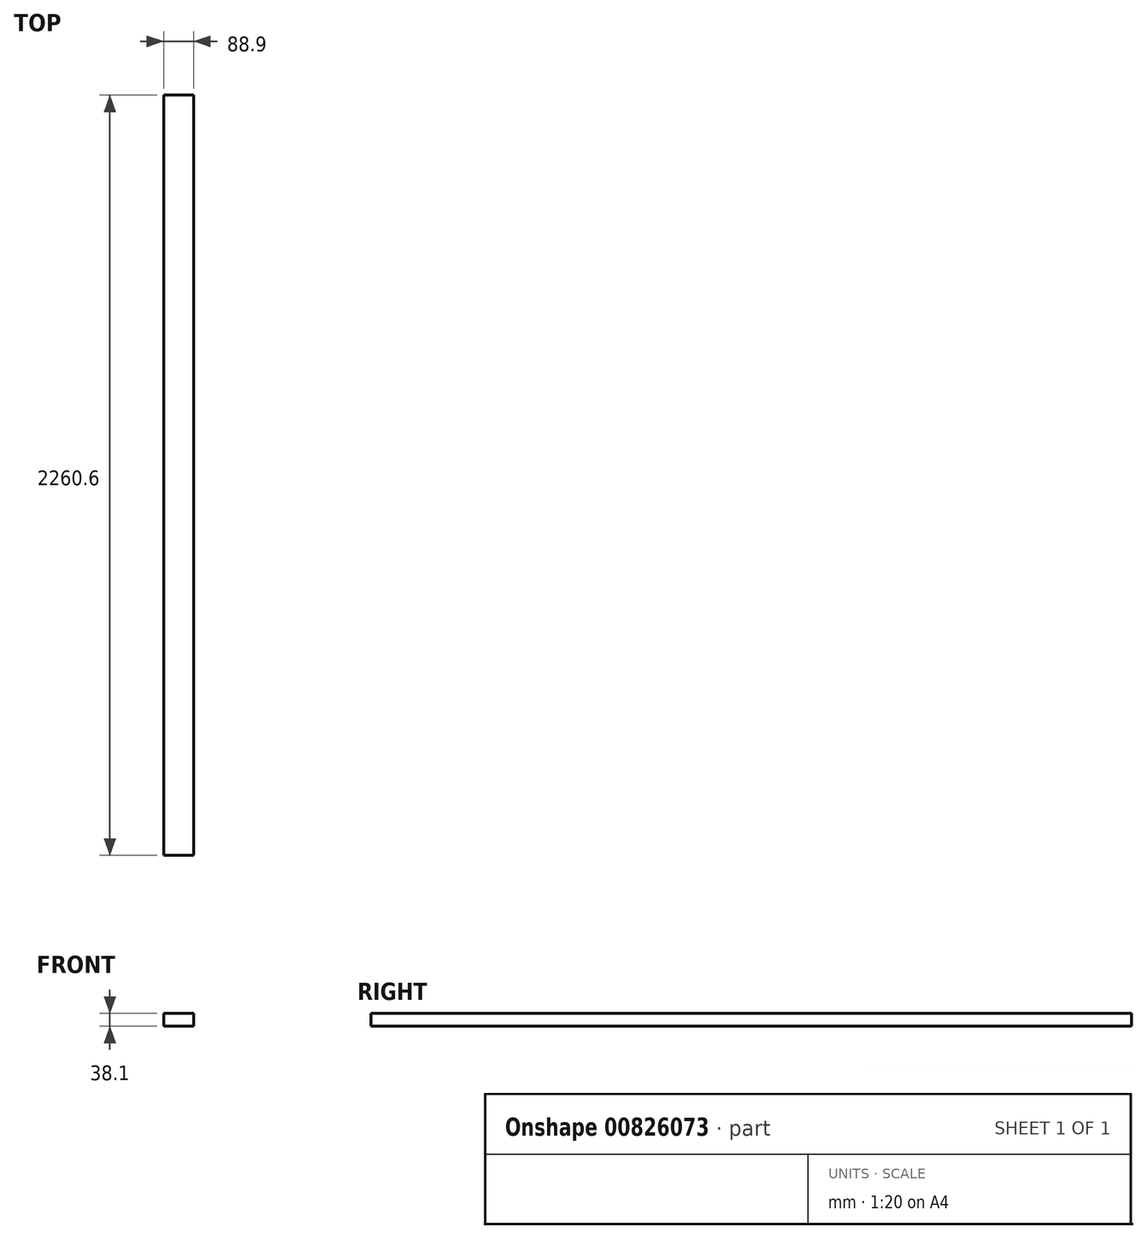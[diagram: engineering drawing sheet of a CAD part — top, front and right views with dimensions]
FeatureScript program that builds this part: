
annotation { "Feature Type Name" : "Feature", "Feature Type Description" : "" }
export const myFeature = defineFeature(function(context is Context, id is Id, definition is map)
    precondition{}
    {
        {
            var Q0;
            Q0=qCreatedBy(makeId("Front.planeOp"),FACE);
            var sketch = newSketch(context, id + "F0", { "sketchPlane" : qUnion([Q0])});
            skLineSegment(sketch, "E0.bottom", {"start": v(0, 0) * mm, "end": v(88.9, 0) * mm});
            skLineSegment(sketch, "E0.top", {"start": v(0, 38.1) * mm, "end": v(88.9, 38.1) * mm});
            skLineSegment(sketch, "E0.left", {"start": v(0, 0) * mm, "end": v(0, 38.1) * mm});
            skLineSegment(sketch, "E0.right", {"start": v(88.9, 0) * mm, "end": v(88.9, 38.1) * mm});
            skSolve(sketch);
        }
        {
            var Q0;
            Q0=qSketchRegion(id+"F0",true);
            extrude(context, id + "F1", {"entities" : qUnion([Q0]), "oppositeDirection" : true, "depth" : 2260.6 * mm, "offsetDistance" : 25.4 * mm});
        }
    });
